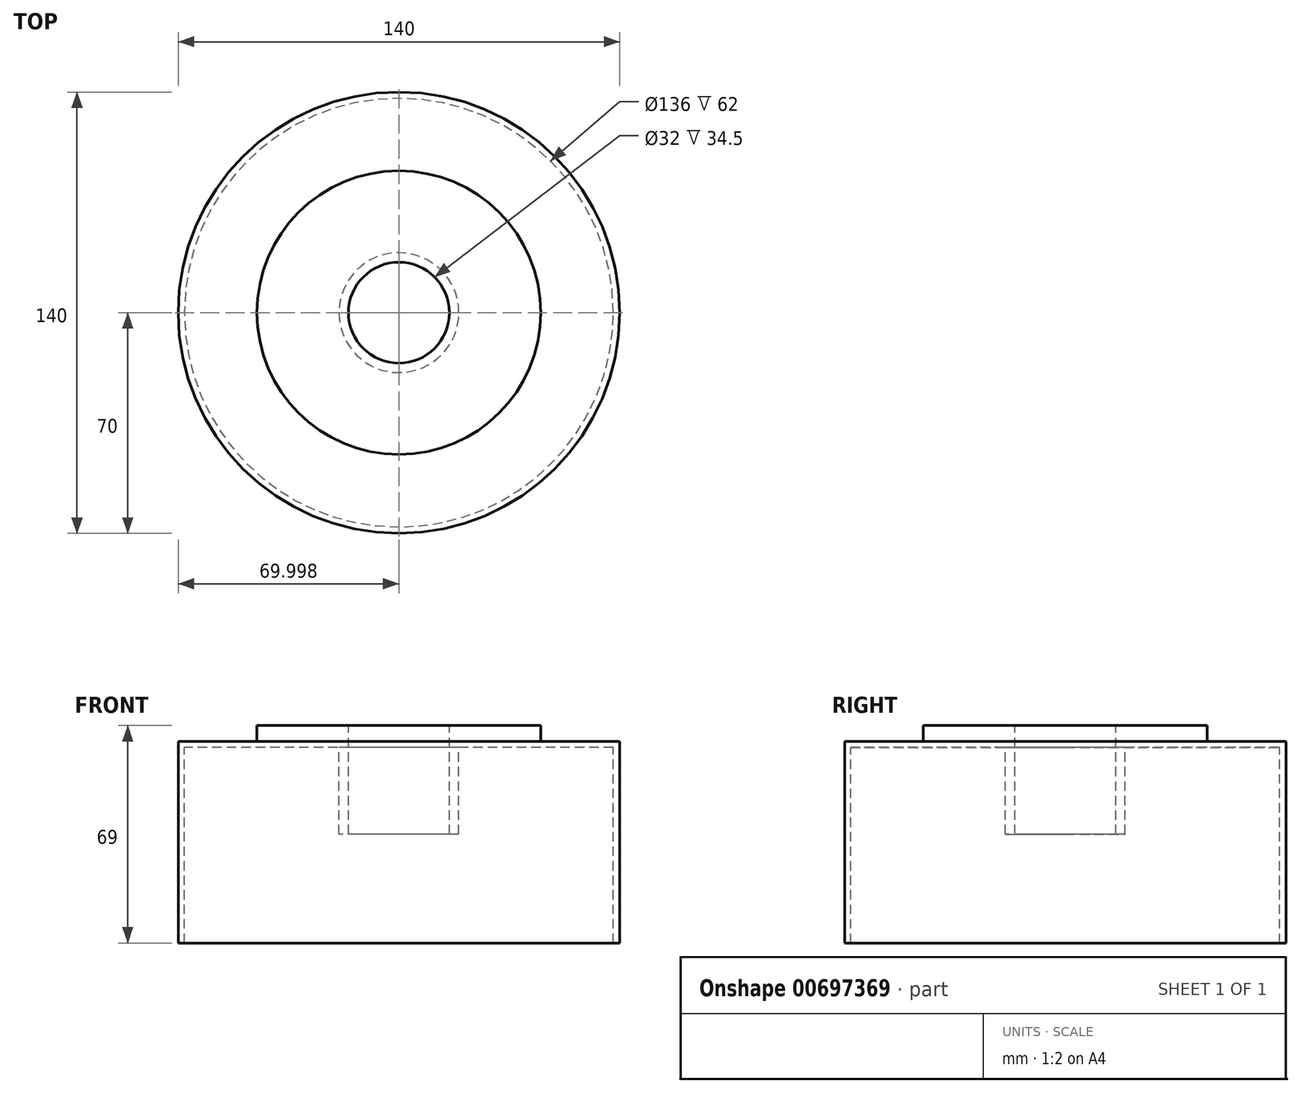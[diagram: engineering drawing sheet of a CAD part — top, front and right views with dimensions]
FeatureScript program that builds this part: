
annotation { "Feature Type Name" : "Feature", "Feature Type Description" : "" }
export const myFeature = defineFeature(function(context is Context, id is Id, definition is map)
    precondition{}
    {
        {
            var Q0;
            Q0=qCreatedBy(makeId("Front.planeOp"),FACE);
            var sketch = newSketch(context, id + "F0", { "sketchPlane" : qUnion([Q0])});
            skLineSegment(sketch, "E0", {"start": v(1.85, -9.24) * mm, "end": v(1.85, -9.24) * mm});
            skLineSegment(sketch, "E1", {"start": v(-70, -34.5) * mm, "end": v(-68, -34.5) * mm});
            skLineSegment(sketch, "E2", {"start": v(-70, -34.5) * mm, "end": v(-70, 29.5) * mm});
            skLineSegment(sketch, "E3", {"start": v(-45, 29.5) * mm, "end": v(-45, 34.5) * mm});
            skLineSegment(sketch, "E4", {"start": v(-45, 34.5) * mm, "end": v(-16, 34.5) * mm});
            skLineSegment(sketch, "E5", {"start": v(-16, 0) * mm, "end": v(-16, 34.5) * mm});
            skLineSegment(sketch, "E6", {"start": v(-68, 27.5) * mm, "end": v(-19, 27.5) * mm});
            skLineSegment(sketch, "E7", {"start": v(-45, 29.5) * mm, "end": v(-70, 29.5) * mm});
            skLineSegment(sketch, "E8", {"start": v(-68, 27.5) * mm, "end": v(-68, -34.5) * mm});
            skLineSegment(sketch, "E9", {"start": v(-19, 27.5) * mm, "end": v(-19, 0) * mm});
            skLineSegment(sketch, "E10", {"start": v(-19, 0) * mm, "end": v(-16, 0) * mm});
            skLineSegment(sketch, "E11", {"start": v(0, 46.58) * mm, "end": v(0, -34.32) * mm});
            skSolve(sketch);
        }
        {
            var Q0;
            Q0 = qSketchRegion(id + "F0", true);
            var Q1;
            Q1=sQuery(id+"F0.wireOp",EDGE,"E11");
            revolve(context, id + "F1", {"entities" : qUnion([Q0]), "axis" : qUnion([Q1]), "revolveType" : RevolveType.FULL});
        }
    });
